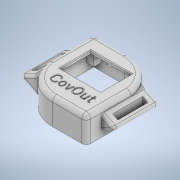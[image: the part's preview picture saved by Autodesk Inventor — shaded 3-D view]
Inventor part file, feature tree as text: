
AUTODESK INVENTOR PART (.ipt)
format: ipt  version: 2020 (Build 240168000, 168)  size: 540,160 bytes
history: native  units: mm
features: other x4, fillet x4, sketch x3, extrude x2, projected_geometry x2, chamfer x1, hole x1
ambient origin geometry x8: Origin, YZ Plane, XZ Plane, XY Plane, X Axis, Y Axis, Z Axis, Center Point
bodies: Body1 (feature_tree)
feature tree (17):
  other  "modelo2bateria.ipt"
  extrude  "Extrusión1"  Depth=10.0mm
  fillet  "Empalme1"  Radius=5.0mm
  fillet  "Empalme2"  Radius=10.0mm
  fillet  "Empalme3"  Radius=2.0mm
  chamfer  "Chaflán1"  Distance=0.5mm Angle=45.0deg
  fillet  "Empalme4"  Radius=3.0mm
  extrude  "Extrusión2"  Depth=4.2mm TaperAngle=0.0deg
  hole  "Agujero1"  [1 undecoded]
  other  "Sólido3::modelo2bateria.ipt"
  other  "OperaciónIdentificador1"
  sketch  "Boceto1"  dims[d0=10.0mm d1=3.0mm d2=5.0mm d3=10.0mm d4=0.0mm d5=2.0mm]
  sketch  "Boceto2"  dims[d6=1.5mm]
  sketch  "Boceto3"  dims[d7=1.5mm d8=0.5mm d9=2.0mm d10=45.0deg d11=3.0mm d12=0.5mm d13=0.0mm d14=1.94056mm d15=3.0mm d16=4.0mm d17=2.0mm d18=90.0deg d19=4.2mm d20=0.0mm]
  projected_geometry  "Contorno proyectado1"
  projected_geometry  "Contorno proyectado2"
  other  "Sólido1"
note: 1 required parameter value undecoded (feature->parameter linkage not recoverable at this tier; creation-order binding heuristic only, values carry confidence <= 0.55)
